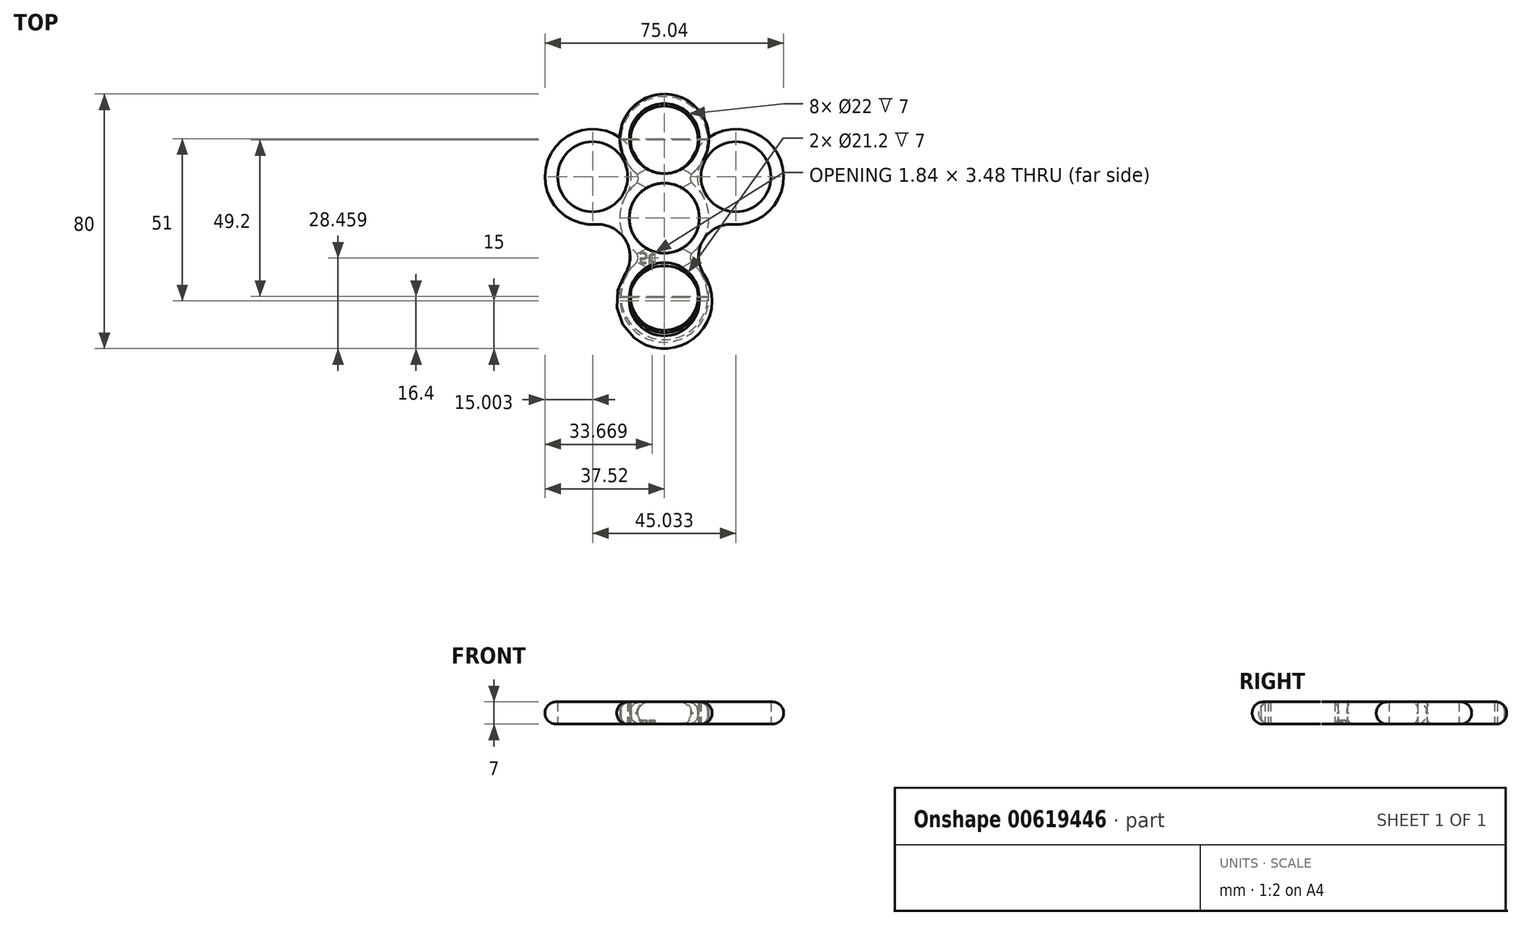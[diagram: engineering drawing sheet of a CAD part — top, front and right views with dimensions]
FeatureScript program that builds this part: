
annotation { "Feature Type Name" : "Feature", "Feature Type Description" : "" }
export const myFeature = defineFeature(function(context is Context, id is Id, definition is map)
    precondition{}
    {
        {
            var Q0;
            Q0=qCreatedBy(makeId("Top.planeOp"),FACE);
            var sketch = newSketch(context, id + "F0", { "sketchPlane" : qUnion([Q0])});
            skCircle(sketch, "E0", {"center": v(0, 0) * mm, "radius": 11 * mm});
            skCircle(sketch, "E1", {"center": v(22.52, 13) * mm, "radius": 11 * mm});
            skCircle(sketch, "E2", {"center": v(22.52, 13) * mm, "radius": 15 * mm});
            skCircle(sketch, "E3.1.0", {"center": v(-22.52, 13) * mm, "radius": 15 * mm});
            skCircle(sketch, "E3.1.1", {"center": v(-22.52, 13) * mm, "radius": 11 * mm});
            skCircle(sketch, "E3.2.0", {"center": v(0, -26) * mm, "radius": 15 * mm});
            skCircle(sketch, "E3.2.1", {"center": v(0, -26) * mm, "radius": 11 * mm});
            skCircle(sketch, "E4", {"center": v(0, 0) * mm, "radius": 13 * mm});
            skCircle(sketch, "E5", {"center": v(0, 24.1) * mm, "radius": 10.1 * mm});
            skCircle(sketch, "E6.1.0", {"center": v(-20.88, -12.05) * mm, "radius": 10.1 * mm});
            skCircle(sketch, "E6.2.0", {"center": v(20.88, -12.05) * mm, "radius": 10.1 * mm});
            skSolve(sketch);
        }
        {
            var Q0;
            {var subQ4=sQuery(id+"F0.wireOp",EDGE,"E3.2.1");Q0=makeQuery(id+"F0.imprint","IMPRINT",FACE,{"disambiguationData":[TD([[makeQuery(id+"F0.imprint","IMPRINT",EDGE,{"derivedFrom":subQ4}),-1.0]])]});}
            var Q1;
            {var subQ0=sQuery(id+"F0.wireOp",EDGE,"E3.1.0");var subQ1=sQuery(id+"F0.wireOp",EDGE,"E0");var subQ2=makeQuery(id+"F0.imprint","INTERSECT",VERTEX,{"derivedFrom":[subQ1,subQ0]});Q1=makeQuery(id+"F0.imprint","IMPRINT",FACE,{"disambiguationData":[TD([[makeQuery(id+"F0.imprint","IMPRINT",EDGE,{"disambiguationData":[TD([[subQ2,-1.0]])],"derivedFrom":subQ1}),-1.0]])]});}
            var Q2;
            {var subQ0=sQuery(id+"F0.wireOp",EDGE,"E2");var subQ1=sQuery(id+"F0.wireOp",EDGE,"E0");var subQ2=makeQuery(id+"F0.imprint","INTERSECT",VERTEX,{"derivedFrom":[subQ1,subQ0]});Q2=makeQuery(id+"F0.imprint","IMPRINT",FACE,{"disambiguationData":[TD([[makeQuery(id+"F0.imprint","IMPRINT",EDGE,{"disambiguationData":[TD([[subQ2,1.0]])],"derivedFrom":subQ1}),-1.0]])]});}
            var Q3;
            {var subQ1=sQuery(id+"F0.wireOp",EDGE,"E1");Q3=makeQuery(id+"F0.imprint","IMPRINT",FACE,{"disambiguationData":[TD([[makeQuery(id+"F0.imprint","IMPRINT",EDGE,{"derivedFrom":subQ1}),-1.0]])]});}
            var Q4;
            {var subQ0=sQuery(id+"F0.wireOp",EDGE,"E2");var subQ1=makeQuery(id+"F0.imprint","INTERSECT",VERTEX,{"derivedFrom":[sQuery(id+"F0.wireOp",EDGE,"E0"),subQ0]});Q4=makeQuery(id+"F0.imprint","IMPRINT",FACE,{"disambiguationData":[TD([[makeQuery(id+"F0.imprint","IMPRINT",EDGE,{"disambiguationData":[TD([[subQ1,1.0]])],"derivedFrom":subQ0}),1.0]])]});}
            var Q5;
            {var subQ0=sQuery(id+"F0.wireOp",EDGE,"E4");var subQ1=sQuery(id+"F0.wireOp",EDGE,"E3.1.0");var subQ2=makeQuery(id+"F0.imprint","INTERSECT",VERTEX,{"disambiguationData":[OD(0.0)],"derivedFrom":[subQ1,subQ0]});Q5=makeQuery(id+"F0.imprint","IMPRINT",FACE,{"disambiguationData":[TD([[makeQuery(id+"F0.imprint","IMPRINT",EDGE,{"disambiguationData":[TD([[subQ2,-1.0]])],"derivedFrom":subQ1}),1.0]])]});}
            var Q6;
            {var subQ0=sQuery(id+"F0.wireOp",EDGE,"E3.1.1");Q6=makeQuery(id+"F0.imprint","IMPRINT",FACE,{"disambiguationData":[TD([[makeQuery(id+"F0.imprint","IMPRINT",EDGE,{"derivedFrom":subQ0}),-1.0]])]});}
            var Q7;
            {var subQ0=sQuery(id+"F0.wireOp",EDGE,"E4");var subQ1=sQuery(id+"F0.wireOp",EDGE,"E3.2.0");var subQ2=makeQuery(id+"F0.imprint","INTERSECT",VERTEX,{"disambiguationData":[OD(0.0)],"derivedFrom":[subQ1,subQ0]});Q7=makeQuery(id+"F0.imprint","IMPRINT",FACE,{"disambiguationData":[TD([[makeQuery(id+"F0.imprint","IMPRINT",EDGE,{"disambiguationData":[TD([[subQ2,-1.0]])],"derivedFrom":subQ1}),1.0]])]});}
            var Q8;
            {var subQ0=sQuery(id+"F0.wireOp",EDGE,"E5");var subQ1=sQuery(id+"F0.wireOp",EDGE,"E2");var subQ2=makeQuery(id+"F0.imprint","INTERSECT",VERTEX,{"derivedFrom":[subQ1,subQ0]});Q8=makeQuery(id+"F0.imprint","IMPRINT",FACE,{"disambiguationData":[TD([[makeQuery(id+"F0.imprint","IMPRINT",EDGE,{"disambiguationData":[TD([[subQ2,-1.0]])],"derivedFrom":subQ1}),-1.0]])]});}
            var Q9;
            {var subQ0=sQuery(id+"F0.wireOp",EDGE,"E3.1.0");var subQ1=sQuery(id+"F0.wireOp",EDGE,"E0");var subQ2=makeQuery(id+"F0.imprint","INTERSECT",VERTEX,{"derivedFrom":[subQ1,subQ0]});Q9=makeQuery(id+"F0.imprint","IMPRINT",FACE,{"disambiguationData":[TD([[makeQuery(id+"F0.imprint","IMPRINT",EDGE,{"disambiguationData":[TD([[subQ2,1.0]])],"derivedFrom":subQ1}),-1.0]])]});}
            var Q10;
            {var subQ0=sQuery(id+"F0.wireOp",EDGE,"E6.1.0");var subQ1=sQuery(id+"F0.wireOp",EDGE,"E3.1.0");var subQ2=makeQuery(id+"F0.imprint","INTERSECT",VERTEX,{"derivedFrom":[subQ1,subQ0]});Q10=makeQuery(id+"F0.imprint","IMPRINT",FACE,{"disambiguationData":[TD([[makeQuery(id+"F0.imprint","IMPRINT",EDGE,{"disambiguationData":[TD([[subQ2,-1.0]])],"derivedFrom":subQ1}),-1.0]])]});}
            var Q11;
            {var subQ0=sQuery(id+"F0.wireOp",EDGE,"E6.2.0");var subQ1=sQuery(id+"F0.wireOp",EDGE,"E2");var subQ2=makeQuery(id+"F0.imprint","INTERSECT",VERTEX,{"derivedFrom":[subQ1,subQ0]});Q11=makeQuery(id+"F0.imprint","IMPRINT",FACE,{"disambiguationData":[TD([[makeQuery(id+"F0.imprint","IMPRINT",EDGE,{"disambiguationData":[TD([[subQ2,1.0]])],"derivedFrom":subQ1}),-1.0]])]});}
            var Q12;
            {var subQ1=sQuery(id+"F0.wireOp",EDGE,"E3.1.0");var subQ6=sQuery(id+"F0.wireOp",EDGE,"E0");var subQ9=makeQuery(id+"F0.imprint","INTERSECT",VERTEX,{"disambiguationData":[OD(1.0)],"derivedFrom":[subQ6,subQ1]});Q12=makeQuery(id+"F0.imprint","IMPRINT",FACE,{"disambiguationData":[TD([[makeQuery(id+"F0.imprint","IMPRINT",EDGE,{"disambiguationData":[TD([[subQ9,-1.0]])],"derivedFrom":subQ6}),-1.0]])]});}
            var Q13;
            {var subQ0=sQuery(id+"F0.wireOp",EDGE,"E6.1.0");var subQ1=sQuery(id+"F0.wireOp",EDGE,"E3.2.0");var subQ2=makeQuery(id+"F0.imprint","INTERSECT",VERTEX,{"derivedFrom":[subQ1,subQ0]});Q13=makeQuery(id+"F0.imprint","IMPRINT",FACE,{"disambiguationData":[TD([[makeQuery(id+"F0.imprint","IMPRINT",EDGE,{"disambiguationData":[TD([[subQ2,1.0]])],"derivedFrom":subQ1}),-1.0]])]});}
            extrude(context, id + "F1", {"entities" : qUnion([Q0, Q1, Q2, Q3, Q4, Q5, Q6, Q7, Q8, Q9, Q10, Q11, Q12, Q13]), "depth" : 7 * mm, "offsetDistance" : 25 * mm});
        }
        {
            var Q0;
            Q0=makeQuery(id+"F1.opExtrude","CAP_EDGE",EDGE,{"disambiguationData":[OSD([sQuery(id+"F0.wireOp",EDGE,"E3.1.0")])],"isStart":false});
            var Q1;
            Q1=makeQuery(id+"F1.opExtrude","CAP_EDGE",EDGE,{"disambiguationData":[OSD([sQuery(id+"F0.wireOp",EDGE,"E3.1.0")])],"isStart":true});
            fillet(context, id + "F2", {"entities" : qUnion([Q0, Q1]), "radius" : 3.5 * mm, "tangentPropagation" : true, "allowEdgeOverflow" : false});
        }
        {
            var Q0;
            Q0=qCreatedBy(makeId("Top.planeOp"),FACE);
            var sketch = newSketch(context, id + "F3", { "sketchPlane" : qUnion([Q0])});
            skCircle(sketch, "E7", {"center": v(0, 0) * mm, "radius": 11 * mm});
            skCircle(sketch, "E8", {"center": v(0, -25) * mm, "radius": 11 * mm});
            skCircle(sketch, "E9", {"center": v(0, -25) * mm, "radius": 14 * mm});
            skCircle(sketch, "E10.1.0", {"center": v(0, 25) * mm, "radius": 14 * mm});
            skCircle(sketch, "E10.1.1", {"center": v(0, 25) * mm, "radius": 11 * mm});
            skCircle(sketch, "E11", {"center": v(0, 0) * mm, "radius": 14 * mm});
            skCircle(sketch, "E12", {"center": v(-10.77, 12.5) * mm, "radius": 2.5 * mm});
            skCircle(sketch, "E13.MirrorC", {"center": v(10.77, 12.5) * mm, "radius": 2.5 * mm});
            skCircle(sketch, "E14.MirrorC", {"center": v(-10.77, -12.5) * mm, "radius": 2.5 * mm});
            skCircle(sketch, "E15.MirrorC", {"center": v(10.77, -12.5) * mm, "radius": 2.5 * mm});
            skSolve(sketch);
        }
        {
            var Q0;
            Q0=makeQuery(id+"F3.imprint","IMPRINT",FACE,{"disambiguationData":[TD([[makeQuery(id+"F3.imprint","IMPRINT",EDGE,{"derivedFrom":sQuery(id+"F3.wireOp",EDGE,"E10.1.1")}),-1.0]])]});
            var Q1;
            Q1=makeQuery(id+"F3.imprint","IMPRINT",FACE,{"disambiguationData":[TD([[makeQuery(id+"F3.imprint","IMPRINT",EDGE,{"derivedFrom":sQuery(id+"F3.wireOp",EDGE,"E8")}),-1.0]])]});
            var Q2;
            {var subQ0=sQuery(id+"F3.wireOp",EDGE,"RRNNmw5K-JgWo-KLzD-V5Yt-wURHGnj7VZe6");var subQ1=sQuery(id+"F3.wireOp",EDGE,"E9");var subQ2=makeQuery(id+"F3.imprint","INTERSECT",VERTEX,{"derivedFrom":[subQ1,subQ0]});Q2=makeQuery(id+"F3.imprint","IMPRINT",FACE,{"disambiguationData":[TD([[makeQuery(id+"F3.imprint","IMPRINT",EDGE,{"disambiguationData":[TD([[subQ2,1.0]])],"derivedFrom":subQ1}),-1.0]])]});}
            var Q3;
            {var subQ4=sQuery(id+"F3.wireOp",EDGE,"E7");var subQ7=sQuery(id+"F3.wireOp",EDGE,"E9");var subQ8=makeQuery(id+"F3.imprint","INTERSECT",VERTEX,{"derivedFrom":[subQ4,subQ7]});Q3=makeQuery(id+"F3.imprint","IMPRINT",FACE,{"disambiguationData":[TD([[makeQuery(id+"F3.imprint","IMPRINT",EDGE,{"disambiguationData":[TD([[subQ8,1.0]])],"derivedFrom":subQ4}),-1.0]])]});}
            var Q4;
            {var subQ0=sQuery(id+"F3.wireOp",EDGE,"E9");var subQ1=makeQuery(id+"F3.imprint","INTERSECT",VERTEX,{"derivedFrom":[sQuery(id+"F3.wireOp",EDGE,"E7"),subQ0]});Q4=makeQuery(id+"F3.imprint","IMPRINT",FACE,{"disambiguationData":[TD([[makeQuery(id+"F3.imprint","IMPRINT",EDGE,{"disambiguationData":[TD([[subQ1,1.0]])],"derivedFrom":subQ0}),1.0]])]});}
            var Q5;
            {var subQ0=sQuery(id+"F3.wireOp",EDGE,"E9");var subQ1=sQuery(id+"F3.wireOp",EDGE,"E7");var subQ2=makeQuery(id+"F3.imprint","INTERSECT",VERTEX,{"derivedFrom":[subQ1,subQ0]});Q5=makeQuery(id+"F3.imprint","IMPRINT",FACE,{"disambiguationData":[TD([[makeQuery(id+"F3.imprint","IMPRINT",EDGE,{"disambiguationData":[TD([[subQ2,-1.0]])],"derivedFrom":subQ1}),-1.0]])]});}
            var Q6;
            {var subQ0=sQuery(id+"F3.wireOp",EDGE,"6frdjyo3-eJqu-CvTG-6SSP-wImGWKrDhhcj");var subQ1=sQuery(id+"F3.wireOp",EDGE,"E9");var subQ2=makeQuery(id+"F3.imprint","INTERSECT",VERTEX,{"derivedFrom":[subQ1,subQ0]});Q6=makeQuery(id+"F3.imprint","IMPRINT",FACE,{"disambiguationData":[TD([[makeQuery(id+"F3.imprint","IMPRINT",EDGE,{"disambiguationData":[TD([[subQ2,-1.0]])],"derivedFrom":subQ1}),-1.0]])]});}
            var Q7;
            {var subQ0=sQuery(id+"F3.wireOp",EDGE,"E10.1.0");var subQ1=makeQuery(id+"F3.imprint","INTERSECT",VERTEX,{"derivedFrom":[sQuery(id+"F3.wireOp",EDGE,"E7"),subQ0]});Q7=makeQuery(id+"F3.imprint","IMPRINT",FACE,{"disambiguationData":[TD([[makeQuery(id+"F3.imprint","IMPRINT",EDGE,{"disambiguationData":[TD([[subQ1,1.0]])],"derivedFrom":subQ0}),1.0]])]});}
            var Q8;
            {var subQ0=sQuery(id+"F3.wireOp",EDGE,"9Xlvclzx-jsLW-KVvu-FAV9-2hRbf2nZq6N0");var subQ1=sQuery(id+"F3.wireOp",EDGE,"E10.1.0");var subQ2=makeQuery(id+"F3.imprint","INTERSECT",VERTEX,{"derivedFrom":[subQ1,subQ0]});Q8=makeQuery(id+"F3.imprint","IMPRINT",FACE,{"disambiguationData":[TD([[makeQuery(id+"F3.imprint","IMPRINT",EDGE,{"disambiguationData":[TD([[subQ2,1.0]])],"derivedFrom":subQ1}),-1.0]])]});}
            var Q9;
            {var subQ0=sQuery(id+"F3.wireOp",EDGE,"7G3LZ8x2-Sk5g-oew9-0Gcr-yVgjqpXIMmb4");var subQ1=sQuery(id+"F3.wireOp",EDGE,"E10.1.0");var subQ2=makeQuery(id+"F3.imprint","INTERSECT",VERTEX,{"derivedFrom":[subQ1,subQ0]});Q9=makeQuery(id+"F3.imprint","IMPRINT",FACE,{"disambiguationData":[TD([[makeQuery(id+"F3.imprint","IMPRINT",EDGE,{"disambiguationData":[TD([[subQ2,-1.0]])],"derivedFrom":subQ1}),-1.0]])]});}
            extrude(context, id + "F4", {"entities" : qUnion([Q0, Q1, Q2, Q3, Q4, Q5, Q6, Q7, Q8, Q9]), "depth" : 7 * mm, "offsetDistance" : 25 * mm});
        }
        {
            var Q0;
            Q0=makeQuery(id+"F4.opExtrude","CAP_EDGE",EDGE,{"disambiguationData":[OSD([sQuery(id+"F3.wireOp",EDGE,"E10.1.0")])],"isStart":false});
            var Q1;
            Q1=makeQuery(id+"F4.opExtrude","CAP_EDGE",EDGE,{"disambiguationData":[OSD([sQuery(id+"F3.wireOp",EDGE,"E10.1.0")])],"isStart":true});
            fillet(context, id + "F5", {"entities" : qUnion([Q0, Q1]), "radius" : 3.5 * mm, "tangentPropagation" : true, "allowEdgeOverflow" : false});
        }
        {
            var Q0;
            Q0=qCreatedBy(makeId("Top.planeOp"),FACE);
            var sketch = newSketch(context, id + "F6", { "sketchPlane" : qUnion([Q0])});
            skCircle(sketch, "E16", {"center": v(0, 0) * mm, "radius": 11 * mm});
            skCircle(sketch, "E17", {"center": v(0, -24.6) * mm, "radius": 10.6 * mm});
            skCircle(sketch, "E18", {"center": v(0, -24.6) * mm, "radius": 13.6 * mm});
            skCircle(sketch, "E19.1.0", {"center": v(0, 24.6) * mm, "radius": 13.6 * mm});
            skCircle(sketch, "E19.1.1", {"center": v(0, 24.6) * mm, "radius": 10.6 * mm});
            skCircle(sketch, "E20", {"center": v(0, 0) * mm, "radius": 14 * mm});
            skPoint(sketch, "E21.center", {"position": v(-5.09, -6.96) * mm});
            skCircle(sketch, "E22", {"center": v(-20.37, 12.69) * mm, "radius": 10 * mm});
            skCircle(sketch, "E23.MirrorC", {"center": v(20.37, 12.69) * mm, "radius": 10 * mm});
            skCircle(sketch, "E24.MirrorC", {"center": v(-20.37, -12.69) * mm, "radius": 10 * mm});
            skCircle(sketch, "E25.MirrorC", {"center": v(20.37, -12.69) * mm, "radius": 10 * mm});
            skText(sketch, "E26", { "text": "5¢", "fontName": "OpenSans-Regular.ttf"});
            const initialGuessF6  = {"E26": [-0.00916, -0.01458, 1, 0, 0.00257]};
            skSetInitialGuess(sketch, initialGuessF6);
            skSolve(sketch);
        }
        {
            var Q0;
            {var subQ0=sQuery(id+"F6.wireOp",EDGE,"E24.MirrorC");var subQ1=sQuery(id+"F6.wireOp",EDGE,"E18");var subQ2=makeQuery(id+"F6.imprint","INTERSECT",VERTEX,{"derivedFrom":[subQ1,subQ0]});Q0=makeQuery(id+"F6.imprint","IMPRINT",FACE,{"disambiguationData":[TD([[makeQuery(id+"F6.imprint","IMPRINT",EDGE,{"disambiguationData":[TD([[subQ2,1.0]])],"derivedFrom":subQ1}),-1.0]])]});}
            var Q1;
            {var subQ4=sQuery(id+"F6.wireOp",EDGE,"E16");var subQ6=sQuery(id+"F6.wireOp",EDGE,"E18");var subQ7=makeQuery(id+"F6.imprint","INTERSECT",VERTEX,{"derivedFrom":[subQ4,subQ6]});Q1=makeQuery(id+"F6.imprint","IMPRINT",FACE,{"disambiguationData":[TD([[makeQuery(id+"F6.imprint","IMPRINT",EDGE,{"disambiguationData":[TD([[subQ7,1.0]])],"derivedFrom":subQ4}),-1.0]])]});}
            var Q2;
            {var subQ0=sQuery(id+"F6.wireOp",EDGE,"E22");var subQ1=sQuery(id+"F6.wireOp",EDGE,"E19.1.0");var subQ2=makeQuery(id+"F6.imprint","INTERSECT",VERTEX,{"derivedFrom":[subQ1,subQ0]});Q2=makeQuery(id+"F6.imprint","IMPRINT",FACE,{"disambiguationData":[TD([[makeQuery(id+"F6.imprint","IMPRINT",EDGE,{"disambiguationData":[TD([[subQ2,-1.0]])],"derivedFrom":subQ1}),-1.0]])]});}
            var Q3;
            {var subQ5=sQuery(id+"F6.wireOp",EDGE,"E19.1.1");Q3=makeQuery(id+"F6.imprint","IMPRINT",FACE,{"disambiguationData":[TD([[makeQuery(id+"F6.imprint","IMPRINT",EDGE,{"derivedFrom":subQ5}),-1.0]])]});}
            var Q4;
            {var subQ0=sQuery(id+"F6.wireOp",EDGE,"E23.MirrorC");var subQ1=sQuery(id+"F6.wireOp",EDGE,"E19.1.0");var subQ2=makeQuery(id+"F6.imprint","INTERSECT",VERTEX,{"derivedFrom":[subQ1,subQ0]});Q4=makeQuery(id+"F6.imprint","IMPRINT",FACE,{"disambiguationData":[TD([[makeQuery(id+"F6.imprint","IMPRINT",EDGE,{"disambiguationData":[TD([[subQ2,1.0]])],"derivedFrom":subQ1}),-1.0]])]});}
            var Q5;
            {var subQ0=sQuery(id+"F6.wireOp",EDGE,"E19.1.0");var subQ1=makeQuery(id+"F6.imprint","INTERSECT",VERTEX,{"derivedFrom":[sQuery(id+"F6.wireOp",EDGE,"E16"),subQ0]});Q5=makeQuery(id+"F6.imprint","IMPRINT",FACE,{"disambiguationData":[TD([[makeQuery(id+"F6.imprint","IMPRINT",EDGE,{"disambiguationData":[TD([[subQ1,1.0]])],"derivedFrom":subQ0}),1.0]])]});}
            var Q6;
            {var subQ1=sQuery(id+"F6.wireOp",EDGE,"E16");var subQ6=sQuery(id+"F6.wireOp",EDGE,"E18");var subQ7=makeQuery(id+"F6.imprint","INTERSECT",VERTEX,{"derivedFrom":[subQ1,subQ6]});Q6=makeQuery(id+"F6.imprint","IMPRINT",FACE,{"disambiguationData":[TD([[makeQuery(id+"F6.imprint","IMPRINT",EDGE,{"disambiguationData":[TD([[subQ7,-1.0]])],"derivedFrom":subQ1}),-1.0]])]});}
            var Q7;
            {var subQ6=sQuery(id+"F6.wireOp",EDGE,"E17");Q7=makeQuery(id+"F6.imprint","IMPRINT",FACE,{"disambiguationData":[TD([[makeQuery(id+"F6.imprint","IMPRINT",EDGE,{"derivedFrom":subQ6}),-1.0]])]});}
            var Q8;
            {var subQ0=sQuery(id+"F6.wireOp",EDGE,"E18");var subQ1=makeQuery(id+"F6.imprint","INTERSECT",VERTEX,{"derivedFrom":[sQuery(id+"F6.wireOp",EDGE,"E16"),subQ0]});Q8=makeQuery(id+"F6.imprint","IMPRINT",FACE,{"disambiguationData":[TD([[makeQuery(id+"F6.imprint","IMPRINT",EDGE,{"disambiguationData":[TD([[subQ1,1.0]])],"derivedFrom":subQ0}),1.0]])]});}
            var Q9;
            {var subQ0=sQuery(id+"F6.wireOp",EDGE,"E25.MirrorC");var subQ1=sQuery(id+"F6.wireOp",EDGE,"E18");var subQ2=makeQuery(id+"F6.imprint","INTERSECT",VERTEX,{"derivedFrom":[subQ1,subQ0]});Q9=makeQuery(id+"F6.imprint","IMPRINT",FACE,{"disambiguationData":[TD([[makeQuery(id+"F6.imprint","IMPRINT",EDGE,{"disambiguationData":[TD([[subQ2,-1.0]])],"derivedFrom":subQ1}),-1.0]])]});}
            var Q10;
            {var subQ0=sQuery(id+"F6.wireOp",EDGE,"E26.sketch_text.stroke-7");Q10=makeQuery(id+"F6.imprint","IMPRINT",FACE,{"disambiguationData":[TD([[makeQuery(id+"F6.imprint","IMPRINT",EDGE,{"derivedFrom":subQ0}),1.0]])]});}
            var Q11;
            {var subQ11=sQuery(id+"F6.wireOp",EDGE,"E26.sketch_text.stroke-2");Q11=makeQuery(id+"F6.imprint","IMPRINT",FACE,{"disambiguationData":[TD([[makeQuery(id+"F6.imprint","IMPRINT",EDGE,{"derivedFrom":subQ11}),-1.0]])]});}
            var Q12;
            {var subQ6=sQuery(id+"F6.wireOp",EDGE,"E26.sketch_text.stroke-0");Q12=makeQuery(id+"F6.imprint","IMPRINT",FACE,{"disambiguationData":[TD([[makeQuery(id+"F6.imprint","IMPRINT",EDGE,{"derivedFrom":subQ6}),-1.0]])]});}
            var Q13;
            {var subQ0=sQuery(id+"F6.wireOp",EDGE,"E26.sketch_text.stroke-6");var subQ1=sQuery(id+"F6.wireOp",EDGE,"E18");var subQ2=makeQuery(id+"F6.imprint","INTERSECT",VERTEX,{"derivedFrom":[subQ1,subQ0]});Q13=makeQuery(id+"F6.imprint","IMPRINT",FACE,{"disambiguationData":[TD([[makeQuery(id+"F6.imprint","IMPRINT",EDGE,{"disambiguationData":[TD([[subQ2,-1.0]])],"derivedFrom":subQ1}),-1.0]])]});}
            var Q14;
            Q14=makeQuery(id+"F6.imprint","IMPRINT",FACE,{"disambiguationData":[TD([[makeQuery(id+"F6.imprint","IMPRINT",EDGE,{"derivedFrom":sQuery(id+"F6.wireOp",EDGE,"E26.sketch_text.stroke-19")}),-1.0]])]});
            var Q15;
            {var subQ0=sQuery(id+"F6.wireOp",EDGE,"E26.sketch_text.stroke-30");Q15=makeQuery(id+"F6.imprint","IMPRINT",FACE,{"disambiguationData":[TD([[makeQuery(id+"F6.imprint","IMPRINT",EDGE,{"derivedFrom":subQ0}),-1.0]])]});}
            var Q16;
            {var subQ0=sQuery(id+"F6.wireOp",EDGE,"E20");var subQ1=sQuery(id+"F6.wireOp",EDGE,"E18");var subQ2=makeQuery(id+"F6.imprint","INTERSECT",VERTEX,{"disambiguationData":[OD(1.0)],"derivedFrom":[subQ1,subQ0]});Q16=makeQuery(id+"F6.imprint","IMPRINT",FACE,{"disambiguationData":[TD([[makeQuery(id+"F6.imprint","IMPRINT",EDGE,{"disambiguationData":[TD([[subQ2,-1.0]])],"derivedFrom":subQ1}),-1.0]])]});}
            var Q17;
            {var subQ0=sQuery(id+"F6.wireOp",EDGE,"E26.sketch_text.stroke-26");Q17=makeQuery(id+"F6.imprint","IMPRINT",FACE,{"disambiguationData":[TD([[makeQuery(id+"F6.imprint","IMPRINT",EDGE,{"derivedFrom":subQ0}),-1.0]])]});}
            extrude(context, id + "F7", {"entities" : qUnion([Q0, Q1, Q2, Q3, Q4, Q5, Q6, Q7, Q8, Q9, Q10, Q11, Q12, Q13, Q14, Q15, Q16, Q17]), "depth" : 7 * mm, "offsetDistance" : 25 * mm});
        }
        {
            var Q0;
            {var subQ0=sQuery(id+"F6.wireOp",EDGE,"E18");Q0=makeQuery(id+"F7.opExtrude","CAP_EDGE",EDGE,{"disambiguationData":[OSD([subQ0]),TDD([makeQuery(id+"F6.imprint","IMPRINT",EDGE,{"disambiguationData":[TD([[makeQuery(id+"F6.imprint","INTERSECT",VERTEX,{"derivedFrom":[subQ0,sQuery(id+"F6.wireOp",EDGE,"E25.MirrorC")]}),1.0]])],"derivedFrom":subQ0})])],"isStart":false});}
            var Q1;
            {var subQ0=sQuery(id+"F6.wireOp",EDGE,"E18");Q1=makeQuery(id+"F7.opExtrude","CAP_EDGE",EDGE,{"disambiguationData":[OSD([subQ0]),TDD([makeQuery(id+"F6.imprint","IMPRINT",EDGE,{"disambiguationData":[TD([[makeQuery(id+"F6.imprint","INTERSECT",VERTEX,{"derivedFrom":[subQ0,sQuery(id+"F6.wireOp",EDGE,"E25.MirrorC")]}),1.0]])],"derivedFrom":subQ0})])],"isStart":true});}
            fillet(context, id + "F8", {"entities" : qUnion([Q0, Q1]), "radius" : 2.5 * mm, "tangentPropagation" : true, "allowEdgeOverflow" : false});
        }
        {
            var Q0;
            Q0=makeQuery(id+"F7.opExtrude","CAP_FACE",FACE,{"disambiguationData":[OSD([sQuery(id+"F6.wireOp",EDGE,"E16"),sQuery(id+"F6.wireOp",EDGE,"E17"),sQuery(id+"F6.wireOp",EDGE,"E18"),sQuery(id+"F6.wireOp",EDGE,"E19.1.0"),sQuery(id+"F6.wireOp",EDGE,"E19.1.1"),sQuery(id+"F6.wireOp",EDGE,"E20"),sQuery(id+"F6.wireOp",EDGE,"E23.MirrorC"),sQuery(id+"F6.wireOp",EDGE,"E22"),sQuery(id+"F6.wireOp",EDGE,"E24.MirrorC"),sQuery(id+"F6.wireOp",EDGE,"E25.MirrorC")])],"isStart":true});
            var sketch = newSketch(context, id + "F9", { "sketchPlane" : qUnion([Q0])});
            skText(sketch, "E27", { "text": "5¢", "fontName": "OpenSans-Regular.ttf"});
            const initialGuessF9  = {"E27": [-0.00792, 0.01085, 1, 0, 0.00341]};
            skSetInitialGuess(sketch, initialGuessF9);
            skSolve(sketch);
        }
        {
            var Q0;
            Q0=makeQuery(id+"F9.imprint","IMPRINT",FACE,{"disambiguationData":[TD([[makeQuery(id+"F9.imprint","IMPRINT",EDGE,{"derivedFrom":sQuery(id+"F9.wireOp",EDGE,"E27.sketch_text.stroke-0")}),-1.0]])]});
            var Q1;
            Q1=makeQuery(id+"F9.imprint","IMPRINT",FACE,{"disambiguationData":[TD([[makeQuery(id+"F9.imprint","IMPRINT",EDGE,{"derivedFrom":sQuery(id+"F9.wireOp",EDGE,"E27.sketch_text.stroke-19")}),-1.0]])]});
            extrude(context, id + "F10", {"entities" : qUnion([Q0, Q1]), "operationType" : NewBodyOperationType.REMOVE, "oppositeDirection" : true, "depth" : .15 * 8 * mm, "offsetDistance" : 25 * mm});
        }
        {
            var Q0;
            Q0=qCreatedBy(makeId("Right.planeOp"),FACE);
            cPlane(context, id + "F11", {"entities" : qUnion([Q0]), "cplaneType" : CPlaneType.OFFSET, "offset" : 26.6 * mm, "width" : 150 * mm, "height" : 150 * mm});
        }
    });
